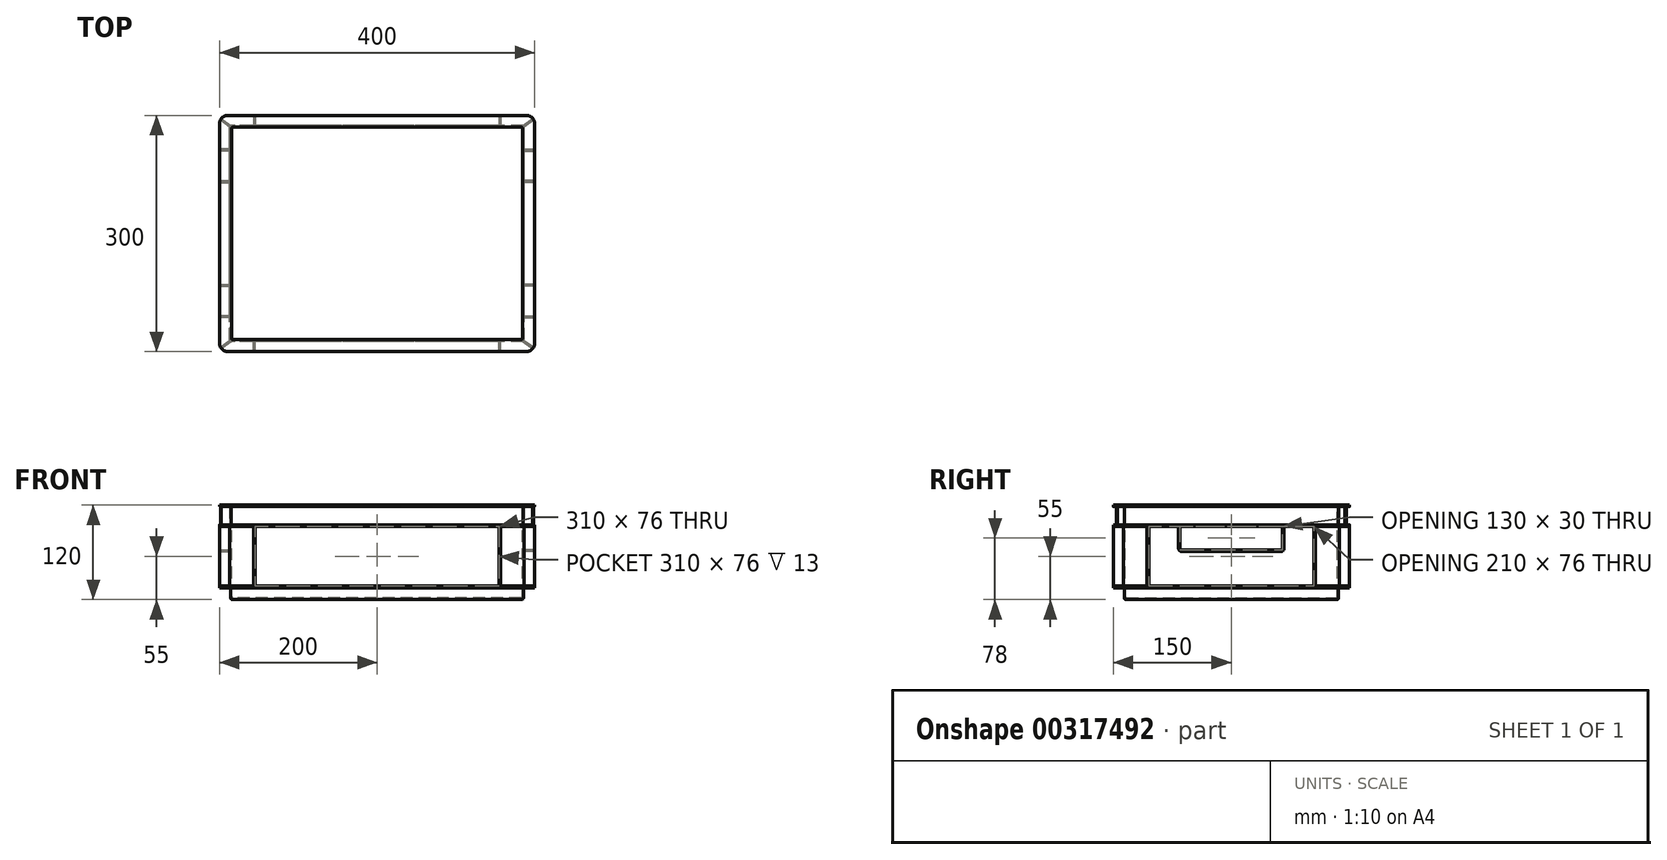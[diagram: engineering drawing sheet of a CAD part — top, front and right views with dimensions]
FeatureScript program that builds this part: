
annotation { "Feature Type Name" : "Feature", "Feature Type Description" : "" }
export const myFeature = defineFeature(function(context is Context, id is Id, definition is map)
    precondition{}
    {
        {
            var Q0;
            Q0=qCreatedBy(makeId("Top.planeOp"),FACE);
            var sketch = newSketch(context, id + "F0", { "sketchPlane" : qUnion([Q0])});
            skLineSegment(sketch, "E0.bottom", {"start": v(186, -136) * mm, "end": v(-186, -136) * mm});
            skLineSegment(sketch, "E0.top", {"start": v(186, 136) * mm, "end": v(-186, 136) * mm});
            skLineSegment(sketch, "E0.left", {"start": v(186, -136) * mm, "end": v(186, 136) * mm});
            skLineSegment(sketch, "E0.right", {"start": v(-186, -136) * mm, "end": v(-186, 136) * mm});
            skPoint(sketch, "E0.middle", {"position": v(0, 0) * mm});
            skPoint(sketch, "E1.visualSharp", {"position": v(-186, 136) * mm});
            skPoint(sketch, "E2.visualSharp", {"position": v(186, 136) * mm});
            skPoint(sketch, "E3.visualSharp", {"position": v(186, -136) * mm});
            skPoint(sketch, "E4.visualSharp", {"position": v(-186, -136) * mm});
            skSolve(sketch);
        }
        {
            var Q0;
            Q0=qSketchRegion(id+"F0",true);
            extrude(context, id + "F1", {"entities" : qUnion([Q0]), "depth" : 15 * mm});
        }
        {
            var Q0;
            Q0=makeQuery(id+"F1.opExtrude","CAP_FACE",FACE,{"disambiguationData":[OSD([sQuery(id+"F0.wireOp",EDGE,"E0.bottom"),sQuery(id+"F0.wireOp",EDGE,"E0.top"),sQuery(id+"F0.wireOp",EDGE,"E0.left"),sQuery(id+"F0.wireOp",EDGE,"E0.right")])],"isStart":false});
            var sketch = newSketch(context, id + "F2", { "sketchPlane" : qUnion([Q0])});
            skLineSegment(sketch, "E5.bottom", {"start": v(190, -150) * mm, "end": v(-190, -150) * mm});
            skLineSegment(sketch, "E5.top", {"start": v(190, 150) * mm, "end": v(-190, 150) * mm});
            skLineSegment(sketch, "E5.left", {"start": v(200, -140) * mm, "end": v(200, 140) * mm});
            skLineSegment(sketch, "E5.right", {"start": v(-200, -140) * mm, "end": v(-200, 140) * mm});
            skPoint(sketch, "E5.middle", {"position": v(0, 0) * mm});
            skPoint(sketch, "E6.visualSharp", {"position": v(-200, 150) * mm});
            skArc(sketch, "E6.filletArc", {"start": v(-190, 150) * mm, "mid": v(-197.07, 147.07) * mm, "end": v(-200, 140) * mm});
            skPoint(sketch, "E7.visualSharp", {"position": v(200, 150) * mm});
            skArc(sketch, "E7.filletArc", {"start": v(200, 140) * mm, "mid": v(197.07, 147.07) * mm, "end": v(190, 150) * mm});
            skPoint(sketch, "E8.visualSharp", {"position": v(200, -150) * mm});
            skArc(sketch, "E8.filletArc", {"start": v(190, -150) * mm, "mid": v(197.07, -147.07) * mm, "end": v(200, -140) * mm});
            skPoint(sketch, "E9.visualSharp", {"position": v(-200, -150) * mm});
            skArc(sketch, "E9.filletArc", {"start": v(-200, -140) * mm, "mid": v(-197.07, -147.07) * mm, "end": v(-190, -150) * mm});
            skSolve(sketch);
        }
        {
            var Q0;
            Q0=makeQuery(id+"F2.imprint","IMPRINT",FACE,{"disambiguationData":[TD([[makeQuery(id+"F2.imprint","IMPRINT",EDGE,{"derivedFrom":makeQuery(id+"F1.opExtrude","CAP_EDGE",EDGE,{"disambiguationData":[OSD([sQuery(id+"F0.wireOp",EDGE,"E0.bottom")])],"isStart":false})}),-1.0]])]});
            var Q1;
            Q1=makeQuery(id+"F2.imprint","IMPRINT",FACE,{"disambiguationData":[TD([[makeQuery(id+"F2.imprint","IMPRINT",EDGE,{"derivedFrom":sQuery(id+"F2.wireOp",EDGE,"E5.bottom")}),-1.0]])]});
            extrude(context, id + "F3", {"entities" : qUnion([Q0, Q1]), "operationType" : NewBodyOperationType.ADD, "depth" : 2 * mm});
        }
        {
            var Q0;
            Q0=makeQuery(id+"F3.opExtrude","CAP_FACE",FACE,{"disambiguationData":[OSD([sQuery(id+"F2.wireOp",EDGE,"E5.bottom"),sQuery(id+"F2.wireOp",EDGE,"E5.top"),sQuery(id+"F2.wireOp",EDGE,"E5.left"),sQuery(id+"F2.wireOp",EDGE,"E5.right"),sQuery(id+"F2.wireOp",EDGE,"E6.filletArc"),sQuery(id+"F2.wireOp",EDGE,"E7.filletArc"),sQuery(id+"F2.wireOp",EDGE,"E8.filletArc"),sQuery(id+"F2.wireOp",EDGE,"E9.filletArc")])],"isStart":false});
            var sketch = newSketch(context, id + "F4", { "sketchPlane" : qUnion([Q0])});
            skLineSegment(sketch, "E10.bottom", {"start": v(187, -137) * mm, "end": v(157, -137) * mm});
            skLineSegment(sketch, "E10.top", {"start": v(187, 137) * mm, "end": v(157, 137) * mm});
            skLineSegment(sketch, "E10.left", {"start": v(187, -137) * mm, "end": v(187, -107) * mm});
            skLineSegment(sketch, "E10.right", {"start": v(-187, -137) * mm, "end": v(-187, -107) * mm});
            skPoint(sketch, "E10.middle", {"position": v(0, 0) * mm});
            skLineSegment(sketch, "E11.bottom", {"start": v(-155, -150) * mm, "end": v(-157, -150) * mm});
            skLineSegment(sketch, "E11.left", {"start": v(-155, -150) * mm, "end": v(-155, -137) * mm});
            skLineSegment(sketch, "E11.right", {"start": v(-157, -150) * mm, "end": v(-157, -137) * mm});
            skPoint(sketch, "E11.middle", {"position": v(-156, -143.5) * mm});
            skLineSegment(sketch, "E12.trimOffspring", {"start": v(-157, -137) * mm, "end": v(-187, -137) * mm});
            skLineSegment(sketch, "E13.bottom", {"start": v(-187, -107) * mm, "end": v(-200, -107) * mm});
            skLineSegment(sketch, "E13.top", {"start": v(-187, -105) * mm, "end": v(-200, -105) * mm});
            skLineSegment(sketch, "E13.right", {"start": v(-200, -107) * mm, "end": v(-200, -105) * mm});
            skPoint(sketch, "E13.middle", {"position": v(-193.5, -106) * mm});
            skLineSegment(sketch, "E14.trimOffspring", {"start": v(-187, -105) * mm, "end": v(-187, 105) * mm});
            skLineSegment(sketch, "E15.MirrorCS", {"start": v(200, -107) * mm, "end": v(200, -105) * mm});
            skLineSegment(sketch, "E16.MirrorCS", {"start": v(155, -150) * mm, "end": v(155, -137) * mm});
            skLineSegment(sketch, "E17.MirrorCS", {"start": v(155, -150) * mm, "end": v(157, -150) * mm});
            skLineSegment(sketch, "E18.MirrorCS", {"start": v(157, -150) * mm, "end": v(157, -137) * mm});
            skLineSegment(sketch, "E19.MirrorCS", {"start": v(187, -105) * mm, "end": v(200, -105) * mm});
            skLineSegment(sketch, "E20.MirrorCS", {"start": v(187, -107) * mm, "end": v(200, -107) * mm});
            skPoint(sketch, "E21.MirrorP", {"position": v(193.5, -106) * mm});
            skLineSegment(sketch, "E22.trimOffspring", {"start": v(187, -105) * mm, "end": v(187, 105) * mm});
            skLineSegment(sketch, "E23.trimOffspring", {"start": v(155, -137) * mm, "end": v(-155, -137) * mm});
            skLineSegment(sketch, "E24.MirrorCS", {"start": v(-200, 107) * mm, "end": v(-200, 105) * mm});
            skPoint(sketch, "E25.MirrorP", {"position": v(-193.5, 106) * mm});
            skLineSegment(sketch, "E26.MirrorCS", {"start": v(-187, 105) * mm, "end": v(-200, 105) * mm});
            skLineSegment(sketch, "E27.MirrorCS", {"start": v(-187, 107) * mm, "end": v(-200, 107) * mm});
            skLineSegment(sketch, "E28.MirrorCS", {"start": v(-155, 150) * mm, "end": v(-157, 150) * mm});
            skLineSegment(sketch, "E29.MirrorCS", {"start": v(-157, 150) * mm, "end": v(-157, 137) * mm});
            skPoint(sketch, "E30.MirrorP", {"position": v(-156, 143.5) * mm});
            skLineSegment(sketch, "E31.MirrorCS", {"start": v(-155, 150) * mm, "end": v(-155, 137) * mm});
            skLineSegment(sketch, "E32.MirrorCS", {"start": v(155, 150) * mm, "end": v(157, 150) * mm});
            skLineSegment(sketch, "E33.MirrorCS", {"start": v(155, 150) * mm, "end": v(155, 137) * mm});
            skLineSegment(sketch, "E34.MirrorCS", {"start": v(157, 150) * mm, "end": v(157, 137) * mm});
            skLineSegment(sketch, "E35.MirrorCS", {"start": v(200, 107) * mm, "end": v(200, 105) * mm});
            skLineSegment(sketch, "E36.MirrorCS", {"start": v(187, 105) * mm, "end": v(200, 105) * mm});
            skPoint(sketch, "E37.MirrorP", {"position": v(193.5, 106) * mm});
            skLineSegment(sketch, "E38.MirrorCS", {"start": v(187, 107) * mm, "end": v(200, 107) * mm});
            skLineSegment(sketch, "E39.trimOffspring", {"start": v(-187, 107) * mm, "end": v(-187, 137) * mm});
            skLineSegment(sketch, "E40.trimOffspring", {"start": v(-157, 137) * mm, "end": v(-187, 137) * mm});
            skLineSegment(sketch, "E41.trimOffspring", {"start": v(155, 137) * mm, "end": v(-155, 137) * mm});
            skLineSegment(sketch, "E42.trimOffspring", {"start": v(187, 107) * mm, "end": v(187, 137) * mm});
            skSolve(sketch);
        }
        {
            var Q0;
            Q0=qSketchRegion(id+"F4",true);
            extrude(context, id + "F5", {"entities" : qUnion([Q0]), "operationType" : NewBodyOperationType.ADD, "depth" : (126 - 50) * mm});
        }
        {
            var Q0;
            Q0=makeQuery(id+"F5.opExtrude","CAP_FACE",FACE,{"disambiguationData":[OSD([sQuery(id+"F4.wireOp",EDGE,"E10.bottom"),sQuery(id+"F4.wireOp",EDGE,"E10.top"),sQuery(id+"F4.wireOp",EDGE,"E10.left"),sQuery(id+"F4.wireOp",EDGE,"E10.right")])],"isStart":false});
            var sketch = newSketch(context, id + "F6", { "sketchPlane" : qUnion([Q0])});
            skArc(sketch, "E43.0", {"start": v(-190, 150) * mm, "mid": v(-197.07, 147.07) * mm, "end": v(-200, 140) * mm});
            skArc(sketch, "E43.1", {"start": v(-200, -140) * mm, "mid": v(-197.07, -147.07) * mm, "end": v(-190, -150) * mm});
            skArc(sketch, "E43.2", {"start": v(190, -150) * mm, "mid": v(197.07, -147.07) * mm, "end": v(200, -140) * mm});
            skArc(sketch, "E43.3", {"start": v(200, 140) * mm, "mid": v(197.07, 147.07) * mm, "end": v(190, 150) * mm});
            skLineSegment(sketch, "E44", {"start": v(-200, 140) * mm, "end": v(-200, -140) * mm});
            skLineSegment(sketch, "E45", {"start": v(-190, -150) * mm, "end": v(190, -150) * mm});
            skLineSegment(sketch, "E46", {"start": v(200, 140) * mm, "end": v(200, -140) * mm});
            skLineSegment(sketch, "E47", {"start": v(-190, 150) * mm, "end": v(190, 150) * mm});
            skSolve(sketch);
        }
        {
            var Q0;
            Q0=qSketchRegion(id+"F6",true);
            extrude(context, id + "F7", {"entities" : qUnion([Q0]), "operationType" : NewBodyOperationType.ADD, "depth" : 2 * mm});
        }
        {
            var Q0;
            Q0=makeQuery(id+"F7.opExtrude","CAP_FACE",FACE,{"disambiguationData":[OSD([sQuery(id+"F6.wireOp",EDGE,"E43.0"),sQuery(id+"F6.wireOp",EDGE,"E43.1"),sQuery(id+"F6.wireOp",EDGE,"E43.2"),sQuery(id+"F6.wireOp",EDGE,"E43.3"),sQuery(id+"F6.wireOp",EDGE,"E44"),sQuery(id+"F6.wireOp",EDGE,"E45"),sQuery(id+"F6.wireOp",EDGE,"E46"),sQuery(id+"F6.wireOp",EDGE,"E47")])],"isStart":false});
            var sketch = newSketch(context, id + "F8", { "sketchPlane" : qUnion([Q0])});
            skLineSegment(sketch, "E48.bottom", {"start": v(185.3, -137) * mm, "end": v(-185.3, -137) * mm});
            skLineSegment(sketch, "E48.top", {"start": v(185.3, 137) * mm, "end": v(-185.3, 137) * mm});
            skLineSegment(sketch, "E48.left", {"start": v(187, -135.76) * mm, "end": v(187, 135.76) * mm});
            skLineSegment(sketch, "E48.right", {"start": v(-187, -135.76) * mm, "end": v(-187, 135.76) * mm});
            skPoint(sketch, "E48.middle", {"position": v(0, 0) * mm});
            skLineSegment(sketch, "E49", {"start": v(-187, 137) * mm, "end": v(187, -137) * mm, "construction": true});
            skLineSegment(sketch, "E50.0", {"start": v(-198.93, 144.5) * mm, "end": v(-187, 135.76) * mm});
            skLineSegment(sketch, "E51.0", {"start": v(-197.85, 146.2) * mm, "end": v(-185.3, 137) * mm});
            skArc(sketch, "E52.0", {"start": v(-197.85, 146.2) * mm, "mid": v(-198.43, 145.37) * mm, "end": v(-198.93, 144.5) * mm});
            skPoint(sketch, "E53.orphan", {"position": v(-190, 150) * mm});
            skPoint(sketch, "E54.orphan", {"position": v(-200, 140) * mm});
            skArc(sketch, "E55.0", {"start": v(197.85, -146.2) * mm, "mid": v(198.43, -145.37) * mm, "end": v(198.93, -144.5) * mm});
            skPoint(sketch, "E56.orphan", {"position": v(200, -140) * mm});
            skPoint(sketch, "E57.orphan", {"position": v(190, -150) * mm});
            skLineSegment(sketch, "E58.trimOffspring", {"start": v(187, -135.76) * mm, "end": v(198.93, -144.5) * mm});
            skLineSegment(sketch, "E59.trimOffspring", {"start": v(185.3, -137) * mm, "end": v(197.85, -146.2) * mm});
            skLineSegment(sketch, "E60.MirrorCS", {"start": v(-197.85, -146.2) * mm, "end": v(-185.3, -137) * mm});
            skPoint(sketch, "E61.MirrorP", {"position": v(-200, -140) * mm});
            skArc(sketch, "E62.MirrorCS", {"start": v(-197.85, -146.2) * mm, "mid": v(-198.43, -145.37) * mm, "end": v(-198.93, -144.5) * mm});
            skLineSegment(sketch, "E63.MirrorCS", {"start": v(-198.93, -144.5) * mm, "end": v(-187, -135.76) * mm});
            skPoint(sketch, "E64.MirrorP", {"position": v(-190, -150) * mm});
            skArc(sketch, "E65.MirrorCS", {"start": v(197.85, 146.2) * mm, "mid": v(198.43, 145.37) * mm, "end": v(198.93, 144.5) * mm});
            skPoint(sketch, "E66.MirrorP", {"position": v(200, 140) * mm});
            skPoint(sketch, "E67.MirrorP", {"position": v(190, 150) * mm});
            skLineSegment(sketch, "E68.MirrorCS", {"start": v(187, 135.76) * mm, "end": v(198.93, 144.5) * mm});
            skLineSegment(sketch, "E69.MirrorCS", {"start": v(185.3, 137) * mm, "end": v(197.85, 146.2) * mm});
            skPoint(sketch, "E70.orphan", {"position": v(187, 137) * mm});
            skPoint(sketch, "E71.orphan", {"position": v(-187, -137) * mm});
            skSolve(sketch);
        }
        {
            var Q0;
            Q0=qSketchRegion(id+"F8",true);
            extrude(context, id + "F9", {"entities" : qUnion([Q0]), "operationType" : NewBodyOperationType.ADD, "depth" : 23 * mm});
        }
        {
            var Q0;
            Q0=makeQuery(id+"F9.opExtrude","CAP_FACE",FACE,{"disambiguationData":[OSD([sQuery(id+"F8.wireOp",EDGE,"E48.bottom"),sQuery(id+"F8.wireOp",EDGE,"E48.top"),sQuery(id+"F8.wireOp",EDGE,"E48.left"),sQuery(id+"F8.wireOp",EDGE,"E48.right"),sQuery(id+"F8.wireOp",EDGE,"E50.0"),sQuery(id+"F8.wireOp",EDGE,"E51.0"),sQuery(id+"F8.wireOp",EDGE,"E52.0"),sQuery(id+"F8.wireOp",EDGE,"E55.0"),sQuery(id+"F8.wireOp",EDGE,"E58.trimOffspring"),sQuery(id+"F8.wireOp",EDGE,"E59.trimOffspring"),sQuery(id+"F8.wireOp",EDGE,"E60.MirrorCS"),sQuery(id+"F8.wireOp",EDGE,"E62.MirrorCS"),sQuery(id+"F8.wireOp",EDGE,"E63.MirrorCS"),sQuery(id+"F8.wireOp",EDGE,"E65.MirrorCS"),sQuery(id+"F8.wireOp",EDGE,"E68.MirrorCS"),sQuery(id+"F8.wireOp",EDGE,"E69.MirrorCS")])],"isStart":false});
            var sketch = newSketch(context, id + "F10", { "sketchPlane" : qUnion([Q0])});
            skArc(sketch, "E72.0", {"start": v(190, -150) * mm, "mid": v(197.07, -147.07) * mm, "end": v(200, -140) * mm});
            skArc(sketch, "E73.0", {"start": v(-200, -140) * mm, "mid": v(-197.07, -147.07) * mm, "end": v(-190, -150) * mm});
            skArc(sketch, "E74.0", {"start": v(200, 140) * mm, "mid": v(197.07, 147.07) * mm, "end": v(190, 150) * mm});
            skLineSegment(sketch, "E75.0", {"start": v(200, -140) * mm, "end": v(200, 140) * mm});
            skLineSegment(sketch, "E76.0", {"start": v(190, 150) * mm, "end": v(-190, 150) * mm});
            skLineSegment(sketch, "E77.0", {"start": v(190, -150) * mm, "end": v(-190, -150) * mm});
            skLineSegment(sketch, "E78.0", {"start": v(-200, -140) * mm, "end": v(-200, 140) * mm});
            skArc(sketch, "E79.0", {"start": v(-190, 150) * mm, "mid": v(-197.07, 147.07) * mm, "end": v(-200, 140) * mm});
            skSolve(sketch);
        }
        {
            var Q0;
            Q0=qSketchRegion(id+"F10",true);
            extrude(context, id + "F11", {"entities" : qUnion([Q0]), "operationType" : NewBodyOperationType.ADD, "depth" : 2 * mm});
        }
        {
            var Q0;
            Q0=makeQuery(id+"F11.opExtrude","CAP_FACE",FACE,{"disambiguationData":[OSD([sQuery(id+"F10.wireOp",EDGE,"E72.0"),sQuery(id+"F10.wireOp",EDGE,"E73.0"),sQuery(id+"F10.wireOp",EDGE,"E74.0"),sQuery(id+"F10.wireOp",EDGE,"E75.0"),sQuery(id+"F10.wireOp",EDGE,"E76.0"),sQuery(id+"F10.wireOp",EDGE,"E77.0"),sQuery(id+"F10.wireOp",EDGE,"E78.0"),sQuery(id+"F10.wireOp",EDGE,"E79.0")])],"isStart":false});
            var sketch = newSketch(context, id + "F12", { "sketchPlane" : qUnion([Q0])});
            skLineSegment(sketch, "E80.bottom", {"start": v(185, -135) * mm, "end": v(-185, -135) * mm});
            skLineSegment(sketch, "E80.top", {"start": v(185, 135) * mm, "end": v(-185, 135) * mm});
            skLineSegment(sketch, "E80.left", {"start": v(185, -135) * mm, "end": v(185, 135) * mm});
            skLineSegment(sketch, "E80.right", {"start": v(-185, -135) * mm, "end": v(-185, 135) * mm});
            skPoint(sketch, "E80.middle", {"position": v(0, 0) * mm});
            skSolve(sketch);
        }
        {
            var Q0;
            Q0=qSketchRegion(id+"F12",true);
            extrude(context, id + "F13", {"entities" : qUnion([Q0]), "operationType" : NewBodyOperationType.REMOVE, "oppositeDirection" : true, "depth" : (168 - 50) * mm});
        }
        {
            var Q0;
            Q0=makeQuery(id+"F5.opExtrude","SWEPT_FACE",FACE,{"disambiguationData":[OSD([sQuery(id+"F4.wireOp",EDGE,"E14.trimOffspring")])]});
            var sketch = newSketch(context, id + "F14", { "sketchPlane" : qUnion([Q0])});
            skLineSegment(sketch, "E81.bottom", {"start": v(63, 61) * mm, "end": v(-63, 61) * mm});
            skLineSegment(sketch, "E81.left", {"start": v(67, 65) * mm, "end": v(67, 93) * mm});
            skLineSegment(sketch, "E81.right", {"start": v(-67, 65) * mm, "end": v(-67, 93) * mm});
            skPoint(sketch, "E81.middle", {"position": v(0, 88.9) * mm});
            skLineSegment(sketch, "E82.bottom", {"start": v(63, 63) * mm, "end": v(-63, 63) * mm});
            skLineSegment(sketch, "E82.left", {"start": v(65, 65) * mm, "end": v(65, 93) * mm});
            skLineSegment(sketch, "E82.right", {"start": v(-65, 65) * mm, "end": v(-65, 93) * mm});
            skLineSegment(sketch, "E83.0", {"start": v(-67, 93) * mm, "end": v(-65, 93) * mm});
            skPoint(sketch, "E84.orphan", {"position": v(-67, 116.8) * mm});
            skPoint(sketch, "E85.orphan", {"position": v(-65, 114.8) * mm});
            skPoint(sketch, "E86.orphan", {"position": v(65, 114.8) * mm});
            skPoint(sketch, "E87.orphan", {"position": v(67, 116.8) * mm});
            skLineSegment(sketch, "E88.trimOffspring", {"start": v(65, 93) * mm, "end": v(67, 93) * mm});
            skPoint(sketch, "E89.orphan", {"position": v(-105, 93) * mm});
            skPoint(sketch, "E90.orphan", {"position": v(105, 93) * mm});
            skPoint(sketch, "E91.visualSharp", {"position": v(-67, 61) * mm});
            skArc(sketch, "E91.filletArc", {"start": v(-67, 65) * mm, "mid": v(-65.83, 62.17) * mm, "end": v(-63, 61) * mm});
            skPoint(sketch, "E92.visualSharp", {"position": v(67, 61) * mm});
            skArc(sketch, "E92.filletArc", {"start": v(63, 61) * mm, "mid": v(65.83, 62.17) * mm, "end": v(67, 65) * mm});
            skPoint(sketch, "E93.visualSharp", {"position": v(65, 63) * mm});
            skArc(sketch, "E93.filletArc", {"start": v(63, 63) * mm, "mid": v(64.41, 63.59) * mm, "end": v(65, 65) * mm});
            skPoint(sketch, "E94.visualSharp", {"position": v(-65, 63) * mm});
            skArc(sketch, "E94.filletArc", {"start": v(-65, 65) * mm, "mid": v(-64.41, 63.59) * mm, "end": v(-63, 63) * mm});
            skSolve(sketch);
        }
        {
            var Q0;
            Q0=qSketchRegion(id+"F14",true);
            var Q1;
            Q1=makeQuery(id+"F7.boolean.opBoolean","MERGE",FACE,{"derivedFrom":[makeQuery(id+"F5.boolean.opBoolean","MERGE",FACE,{"derivedFrom":[makeQuery(id+"F3.opExtrude","SWEPT_FACE",FACE,{"disambiguationData":[OSD([sQuery(id+"F2.wireOp",EDGE,"E5.right")])]}),makeQuery(id+"F5.opExtrude","SWEPT_FACE",FACE,{"disambiguationData":[OSD([sQuery(id+"F4.wireOp",EDGE,"E13.right")])]}),makeQuery(id+"F5.opExtrude","SWEPT_FACE",FACE,{"disambiguationData":[OSD([sQuery(id+"F4.wireOp",EDGE,"E24.MirrorCS")])]})]}),makeQuery(id+"F7.opExtrude","SWEPT_FACE",FACE,{"disambiguationData":[OSD([sQuery(id+"F6.wireOp",EDGE,"E44")])]})]});
            extrude(context, id + "F15", {"entities" : qUnion([Q0]), "operationType" : NewBodyOperationType.ADD, "endBound" : BoundingType.UP_TO_SURFACE, "endBoundEntityFace" : qUnion([Q1]), "depth" : 25 * mm});
        }
        {
            var Q0;
            Q0=makeQuery(id+"F5.opExtrude","SWEPT_FACE",FACE,{"disambiguationData":[OSD([sQuery(id+"F4.wireOp",EDGE,"E22.trimOffspring")])]});
            var sketch = newSketch(context, id + "F16", { "sketchPlane" : qUnion([Q0])});
            skLineSegment(sketch, "E95.0", {"start": v(67, 65) * mm, "end": v(67, 93) * mm});
            skArc(sketch, "E95.1", {"start": v(67, 65) * mm, "mid": v(65.83, 62.17) * mm, "end": v(63, 61) * mm});
            skLineSegment(sketch, "E95.2", {"start": v(-63, 61) * mm, "end": v(63, 61) * mm});
            skLineSegment(sketch, "E95.3", {"start": v(-63, 63) * mm, "end": v(63, 63) * mm});
            skLineSegment(sketch, "E95.4", {"start": v(65, 65) * mm, "end": v(65, 93) * mm});
            skArc(sketch, "E95.5", {"start": v(65, 65) * mm, "mid": v(64.41, 63.59) * mm, "end": v(63, 63) * mm});
            skArc(sketch, "E95.6", {"start": v(-63, 63) * mm, "mid": v(-64.41, 63.59) * mm, "end": v(-65, 65) * mm});
            skArc(sketch, "E95.7", {"start": v(-63, 61) * mm, "mid": v(-65.83, 62.17) * mm, "end": v(-67, 65) * mm});
            skLineSegment(sketch, "E95.8", {"start": v(-67, 65) * mm, "end": v(-67, 93) * mm});
            skLineSegment(sketch, "E95.9", {"start": v(-65, 65) * mm, "end": v(-65, 93) * mm});
            skLineSegment(sketch, "E96", {"start": v(67, 93) * mm, "end": v(65, 93) * mm});
            skLineSegment(sketch, "E97", {"start": v(-65, 93) * mm, "end": v(-67, 93) * mm});
            skSolve(sketch);
        }
        {
            var Q0;
            Q0=qSketchRegion(id+"F16",true);
            var Q1;
            Q1=makeQuery(id+"F7.boolean.opBoolean","MERGE",FACE,{"derivedFrom":[makeQuery(id+"F5.boolean.opBoolean","MERGE",FACE,{"derivedFrom":[makeQuery(id+"F3.opExtrude","SWEPT_FACE",FACE,{"disambiguationData":[OSD([sQuery(id+"F2.wireOp",EDGE,"E5.left")])]}),makeQuery(id+"F5.opExtrude","SWEPT_FACE",FACE,{"disambiguationData":[OSD([sQuery(id+"F4.wireOp",EDGE,"E15.MirrorCS")])]}),makeQuery(id+"F5.opExtrude","SWEPT_FACE",FACE,{"disambiguationData":[OSD([sQuery(id+"F4.wireOp",EDGE,"E35.MirrorCS")])]})]}),makeQuery(id+"F7.opExtrude","SWEPT_FACE",FACE,{"disambiguationData":[OSD([sQuery(id+"F6.wireOp",EDGE,"E46")])]})]});
            extrude(context, id + "F17", {"entities" : qUnion([Q0]), "operationType" : NewBodyOperationType.ADD, "endBound" : BoundingType.UP_TO_SURFACE, "endBoundEntityFace" : qUnion([Q1]), "depth" : 25 * mm});
        }
        {
            var Q0;
            Q0=makeQuery(id+"F13.boolean.opBoolean","COPY",EDGE,{"derivedFrom":makeQuery(id+"F13.opExtrude","SWEPT_EDGE",EDGE,{"disambiguationData":[OSD([sQuery(id+"F12.wireOp",EDGE,"E80.bottom"),sQuery(id+"F12.wireOp",EDGE,"E80.right")])]})});
            var Q1;
            Q1=makeQuery(id+"F13.boolean.opBoolean","COPY",EDGE,{"derivedFrom":makeQuery(id+"F13.opExtrude","SWEPT_EDGE",EDGE,{"disambiguationData":[OSD([sQuery(id+"F12.wireOp",EDGE,"E80.bottom"),sQuery(id+"F12.wireOp",EDGE,"E80.left")])]})});
            var Q2;
            Q2=makeQuery(id+"F13.boolean.opBoolean","COPY",EDGE,{"derivedFrom":makeQuery(id+"F13.opExtrude","SWEPT_EDGE",EDGE,{"disambiguationData":[OSD([sQuery(id+"F12.wireOp",EDGE,"E80.top"),sQuery(id+"F12.wireOp",EDGE,"E80.left")])]})});
            var Q3;
            Q3=makeQuery(id+"F13.boolean.opBoolean","COPY",EDGE,{"derivedFrom":makeQuery(id+"F13.opExtrude","CAP_EDGE",EDGE,{"disambiguationData":[OSD([sQuery(id+"F12.wireOp",EDGE,"E80.top")])],"isStart":false})});
            var Q4;
            Q4=makeQuery(id+"F13.boolean.opBoolean","COPY",EDGE,{"derivedFrom":makeQuery(id+"F13.opExtrude","CAP_EDGE",EDGE,{"disambiguationData":[OSD([sQuery(id+"F12.wireOp",EDGE,"E80.left")])],"isStart":false})});
            var Q5;
            Q5=makeQuery(id+"F13.boolean.opBoolean","COPY",EDGE,{"derivedFrom":makeQuery(id+"F13.opExtrude","CAP_EDGE",EDGE,{"disambiguationData":[OSD([sQuery(id+"F12.wireOp",EDGE,"E80.bottom")])],"isStart":false})});
            var Q6;
            Q6=makeQuery(id+"F13.boolean.opBoolean","COPY",EDGE,{"derivedFrom":makeQuery(id+"F13.opExtrude","CAP_EDGE",EDGE,{"disambiguationData":[OSD([sQuery(id+"F12.wireOp",EDGE,"E80.right")])],"isStart":false})});
            var Q7;
            Q7=makeQuery(id+"F13.boolean.opBoolean","COPY",EDGE,{"derivedFrom":makeQuery(id+"F13.opExtrude","SWEPT_EDGE",EDGE,{"disambiguationData":[OSD([sQuery(id+"F12.wireOp",EDGE,"E80.top"),sQuery(id+"F12.wireOp",EDGE,"E80.right")])]})});
            var Q8;
            Q8=makeQuery(id+"F5.opExtrude","SWEPT_EDGE",EDGE,{"disambiguationData":[OSD([sQuery(id+"F4.wireOp",EDGE,"E10.bottom"),sQuery(id+"F4.wireOp",EDGE,"E10.left")])]});
            var Q9;
            Q9=makeQuery(id+"F5.opExtrude","SWEPT_EDGE",EDGE,{"disambiguationData":[OSD([sQuery(id+"F4.wireOp",EDGE,"E10.top"),sQuery(id+"F4.wireOp",EDGE,"E42.trimOffspring")])]});
            var Q10;
            Q10=makeQuery(id+"F5.opExtrude","SWEPT_EDGE",EDGE,{"disambiguationData":[OSD([sQuery(id+"F4.wireOp",EDGE,"E39.trimOffspring"),sQuery(id+"F4.wireOp",EDGE,"E40.trimOffspring")])]});
            var Q11;
            Q11=makeQuery(id+"F5.opExtrude","SWEPT_EDGE",EDGE,{"disambiguationData":[OSD([sQuery(id+"F4.wireOp",EDGE,"E10.right"),sQuery(id+"F4.wireOp",EDGE,"E12.trimOffspring")])]});
            var Q12;
            Q12=makeQuery(id+"F1.opExtrude","CAP_EDGE",EDGE,{"disambiguationData":[OSD([sQuery(id+"F0.wireOp",EDGE,"E0.left")])],"isStart":true});
            var Q13;
            Q13=makeQuery(id+"F1.opExtrude","CAP_EDGE",EDGE,{"disambiguationData":[OSD([sQuery(id+"F0.wireOp",EDGE,"E0.top")])],"isStart":true});
            var Q14;
            Q14=makeQuery(id+"F1.opExtrude","SWEPT_EDGE",EDGE,{"disambiguationData":[OSD([sQuery(id+"F0.wireOp",EDGE,"E0.top"),sQuery(id+"F0.wireOp",EDGE,"E0.left")])]});
            var Q15;
            Q15=makeQuery(id+"F1.opExtrude","CAP_EDGE",EDGE,{"disambiguationData":[OSD([sQuery(id+"F0.wireOp",EDGE,"E0.bottom")])],"isStart":true});
            var Q16;
            Q16=makeQuery(id+"F1.opExtrude","SWEPT_EDGE",EDGE,{"disambiguationData":[OSD([sQuery(id+"F0.wireOp",EDGE,"E0.bottom"),sQuery(id+"F0.wireOp",EDGE,"E0.left")])]});
            var Q17;
            Q17=makeQuery(id+"F1.opExtrude","SWEPT_EDGE",EDGE,{"disambiguationData":[OSD([sQuery(id+"F0.wireOp",EDGE,"E0.bottom"),sQuery(id+"F0.wireOp",EDGE,"E0.right")])]});
            var Q18;
            Q18=makeQuery(id+"F1.opExtrude","CAP_EDGE",EDGE,{"disambiguationData":[OSD([sQuery(id+"F0.wireOp",EDGE,"E0.right")])],"isStart":true});
            var Q19;
            Q19=makeQuery(id+"F1.opExtrude","SWEPT_EDGE",EDGE,{"disambiguationData":[OSD([sQuery(id+"F0.wireOp",EDGE,"E0.top"),sQuery(id+"F0.wireOp",EDGE,"E0.right")])]});
            fillet(context, id + "F18", {"entities" : qUnion([Q0, Q1, Q2, Q3, Q4, Q5, Q6, Q7, Q8, Q9, Q10, Q11, Q12, Q13, Q14, Q15, Q16, Q17, Q18, Q19]), "radius" : 2 * mm, "tangentPropagation" : true, "allowEdgeOverflow" : false});
        }
    });
